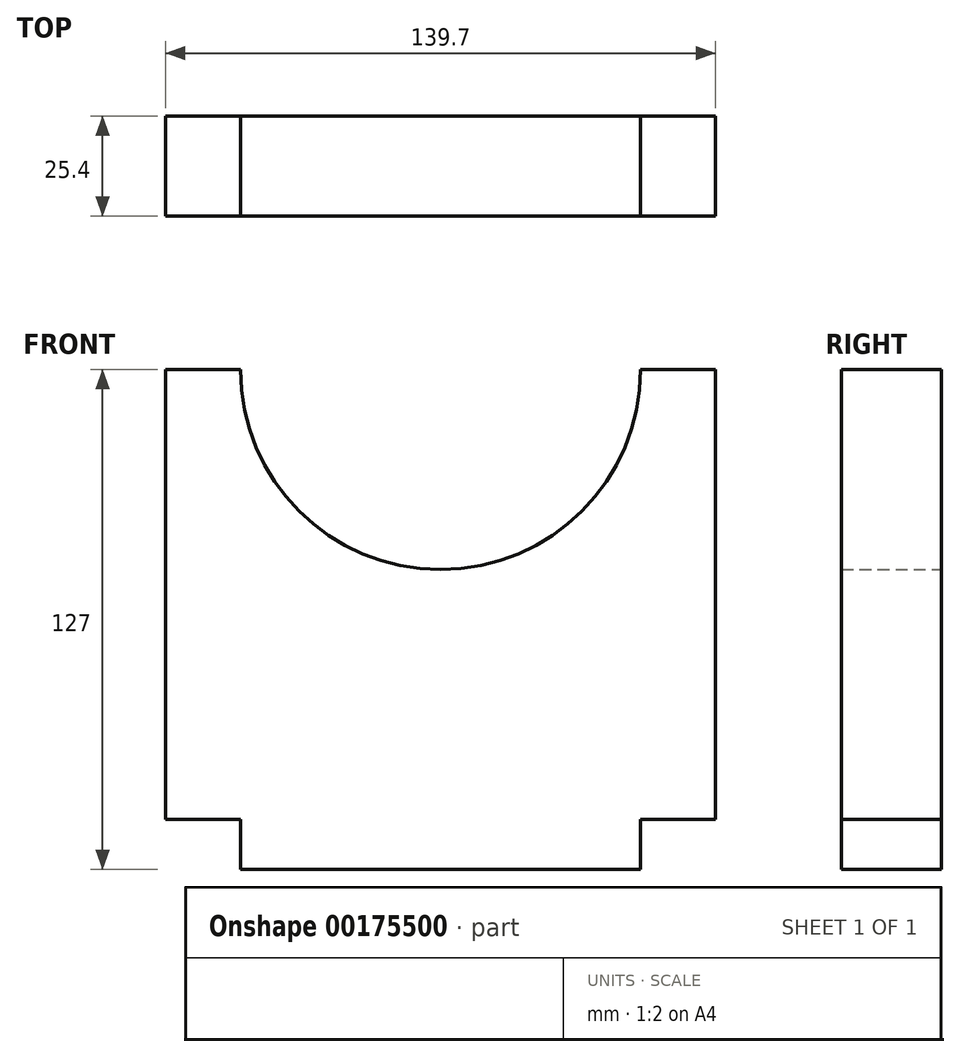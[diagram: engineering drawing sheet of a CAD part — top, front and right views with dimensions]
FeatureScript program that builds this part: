
annotation { "Feature Type Name" : "Feature", "Feature Type Description" : "" }
export const myFeature = defineFeature(function(context is Context, id is Id, definition is map)
    precondition{}
    {
        {
            var Q0;
            Q0=qCreatedBy(makeId("Front.planeOp"),FACE);
            var sketch = newSketch(context, id + "F0", { "sketchPlane" : qUnion([Q0])});
            skLineSegment(sketch, "E0.bottom", {"start": v(69.85, 57.15) * mm, "end": v(50.8, 57.15) * mm});
            skLineSegment(sketch, "E0.top", {"start": v(69.85, -57.15) * mm, "end": v(-69.85, -57.15) * mm});
            skLineSegment(sketch, "E0.left", {"start": v(69.85, 57.15) * mm, "end": v(69.85, -57.15) * mm});
            skLineSegment(sketch, "E0.right", {"start": v(-69.85, 57.15) * mm, "end": v(-69.85, -57.15) * mm});
            skPoint(sketch, "E0.middle", {"position": v(0, 0) * mm});
            skLineSegment(sketch, "E1", {"start": v(-69.85, 57.15) * mm, "end": v(-50.8, 57.15) * mm});
            skLineSegment(sketch, "E2", {"start": v(0, 57.15) * mm, "end": v(0, 6.35) * mm});
            skPoint(sketch, "E2.endSnap0", {"position": v(0, 57.15) * mm});
            skArc(sketch, "E3", {"start": v(-50.8, 57.15) * mm, "mid": v(0, 6.35) * mm, "end": v(50.8, 57.15) * mm});
            skLineSegment(sketch, "E4.trimOffspring", {"start": v(-50.8, 57.15) * mm, "end": v(-69.85, 57.15) * mm});
            skLineSegment(sketch, "E5", {"start": v(-50.8, -57.15) * mm, "end": v(50.8, -57.15) * mm});
            skLineSegment(sketch, "E6.top", {"start": v(-50.8, -69.85) * mm, "end": v(50.8, -69.85) * mm});
            skLineSegment(sketch, "E6.left", {"start": v(-50.8, -57.15) * mm, "end": v(-50.8, -69.85) * mm});
            skLineSegment(sketch, "E6.right", {"start": v(50.8, -57.15) * mm, "end": v(50.8, -69.85) * mm});
            skSolve(sketch);
        }
        {
            var Q0;
            Q0 = qSketchRegion(id + "F0", true);
            extrude(context, id + "F1", {"entities" : qUnion([Q0]), "depth" : 25.4 * mm});
        }
    });
